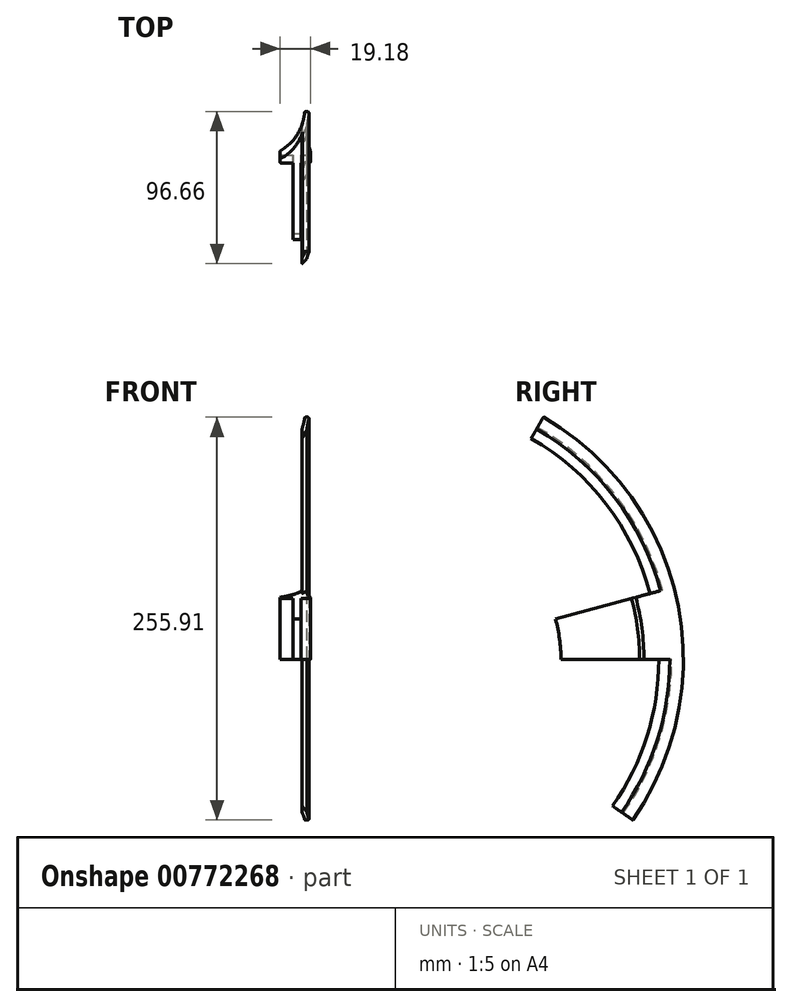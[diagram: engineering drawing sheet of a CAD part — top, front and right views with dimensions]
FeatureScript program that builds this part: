
annotation { "Feature Type Name" : "Feature", "Feature Type Description" : "" }
export const myFeature = defineFeature(function(context is Context, id is Id, definition is map)
    precondition{}
    {
        {
            var Q0;
            Q0=qCreatedBy(makeId("Top.planeOp"),FACE);
            var sketch = newSketch(context, id + "F0", { "sketchPlane" : qUnion([Q0])});
            skFitSpline(sketch, "E0", {"points": [v(-56.77, 9.45) * mm, v(-61.9, -5.76) * mm, v(-72.5, -15.56) * mm], "startDerivative": vector(-3.64, -32.31) * mm, "endDerivative": vector(-29.6, -17.94) * mm});
            skLineSegment(sketch, "E1.bottom", {"start": v(-56.33, 9.46) * mm, "end": v(-55.2, 9.49) * mm});
            skLineSegment(sketch, "E2.top", {"start": v(-71.5, -18.28) * mm, "end": v(-54.3, -18.28) * mm});
            skLineSegment(sketch, "E2.left", {"start": v(-72.5, -15.56) * mm, "end": v(-72.5, -17.28) * mm});
            skLineSegment(sketch, "E2.right", {"start": v(-53.3, -15.56) * mm, "end": v(-53.3, -17.28) * mm});
            skFitSpline(sketch, "E3", {"points": [v(-53.95, 9.51) * mm, v(-55.58, -4.57) * mm, v(-53.3, -15.56) * mm], "startDerivative": vector(-5.89, -27.4) * mm, "endDerivative": vector(6.13, -22.65) * mm});
            skLineSegment(sketch, "E4", {"start": v(-49.82, -168.28) * mm, "end": v(-75.4, -168.28) * mm});
            skPoint(sketch, "E5.visualSharp", {"position": v(-72.5, -18.28) * mm});
            skArc(sketch, "E5.filletArc", {"start": v(-72.5, -17.28) * mm, "mid": v(-72.2, -17.99) * mm, "end": v(-71.5, -18.28) * mm});
            skPoint(sketch, "E6.visualSharp", {"position": v(-53.3, -18.28) * mm});
            skArc(sketch, "E6.filletArc", {"start": v(-54.3, -18.28) * mm, "mid": v(-53.6, -17.99) * mm, "end": v(-53.3, -17.28) * mm});
            skArc(sketch, "E7.filletArc", {"start": v(-56.33, 9.46) * mm, "mid": v(-56.66, 9.33) * mm, "end": v(-56.82, 9.02) * mm});
            skArc(sketch, "E8.filletArc", {"start": v(-54.2, 8.28) * mm, "mid": v(-54.42, 9.13) * mm, "end": v(-55.2, 9.49) * mm});
            skFitSpline(sketch, "E9.0", {"points": [v(-56.88, 10.14) * mm, v(-57.13, 8.98) * mm, v(-57.6, 6.64) * mm, v(-58.2, 3.1) * mm, v(-58.52, 0.16) * mm, v(-58.62, -2.18) * mm, v(-58.62, -3.93) * mm, v(-58.52, -5.66) * mm, v(-58.32, -7.34) * mm, v(-58.05, -8.95) * mm, v(-57.62, -11.04) * mm, v(-56.98, -13.53) * mm, v(-56.45, -15.42) * mm, v(-56.2, -16.34) * mm]});
            skFitSpline(sketch, "E9.1", {"points": [v(-53.79, 9.12) * mm, v(-54.11, 6.21) * mm, v(-55.07, 1.9) * mm, v(-57.14, -3.4) * mm, v(-59.07, -7.06) * mm, v(-61.38, -10.32) * mm, v(-64.09, -13.19) * mm, v(-67.23, -15.75) * mm, v(-69.64, -17.34) * mm, v(-70.94, -18.12) * mm]});
            skLineSegment(sketch, "E9.2", {"start": v(-66.72, -15.28) * mm, "end": v(-56.5, -15.28) * mm});
            skLineSegment(sketch, "E10.bottom", {"start": v(-59.13, -18.28) * mm, "end": v(-64.13, -18.28) * mm});
            skLineSegment(sketch, "E10.top", {"start": v(-59.13, -68.28) * mm, "end": v(-64.13, -68.28) * mm});
            skLineSegment(sketch, "E10.left", {"start": v(-59.13, -18.28) * mm, "end": v(-59.13, -68.28) * mm});
            skLineSegment(sketch, "E10.right", {"start": v(-64.13, -18.28) * mm, "end": v(-64.13, -68.28) * mm});
            skSolve(sketch);
        }
        {
            var Q0;
            Q0=makeQuery(id+"F0.imprint","IMPRINT",FACE,{"disambiguationData":[TD([[makeQuery(id+"F0.imprint","IMPRINT",EDGE,{"derivedFrom":sQuery(id+"F0.wireOp",EDGE,"E0")}),1.0]])]});
            var Q1;
            Q1=sQuery(id+"F0.wireOp",EDGE,"E4");
            revolve(context, id + "F1", {"surfaceOperationType" : NewSurfaceOperationType.NEW, "entities" : qUnion([Q0]), "axis" : qUnion([Q1]), "revolveType" : RevolveType.ONE_DIRECTION, "angle" : 35 * degree});
        }
        {
            var Q0;
            Q0 = qSketchRegion(id + "F0", true);
            var Q1;
            Q1=sQuery(id+"F0.wireOp",EDGE,"E4");
            revolve(context, id + "F2", {"operationType" : NewBodyOperationType.ADD, "surfaceOperationType" : NewSurfaceOperationType.NEW, "entities" : qUnion([Q0]), "axis" : qUnion([Q1]), "revolveType" : RevolveType.ONE_DIRECTION, "oppositeDirection" : true, "angle" : 15 * degree});
        }
        {
            var Q0;
            Q0=makeQuery(id+"F0.imprint","IMPRINT",FACE,{"disambiguationData":[TD([[makeQuery(id+"F0.imprint","IMPRINT",EDGE,{"derivedFrom":sQuery(id+"F0.wireOp",EDGE,"E0")}),1.0]])]});
            var Q1;
            Q1=sQuery(id+"F0.wireOp",EDGE,"E4");
            revolve(context, id + "F3", {"operationType" : NewBodyOperationType.ADD, "surfaceOperationType" : NewSurfaceOperationType.NEW, "entities" : qUnion([Q0]), "axis" : qUnion([Q1]), "revolveType" : RevolveType.ONE_DIRECTION, "oppositeDirection" : true, "angle" : 60 * degree});
        }
    });
